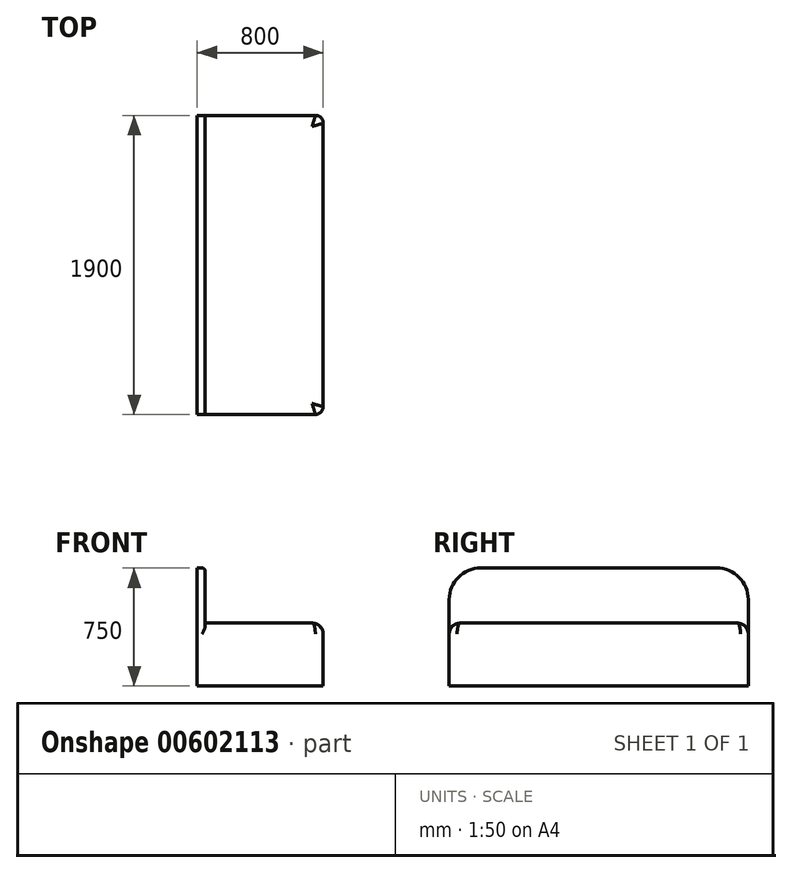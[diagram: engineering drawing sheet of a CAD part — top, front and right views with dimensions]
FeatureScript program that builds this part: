
annotation { "Feature Type Name" : "Feature", "Feature Type Description" : "" }
export const myFeature = defineFeature(function(context is Context, id is Id, definition is map)
    precondition{}
    {
        {
            var Q0;
            Q0=qCreatedBy(makeId("Top.planeOp"),FACE);
            var sketch = newSketch(context, id + "F0", { "sketchPlane" : qUnion([Q0])});
            skLineSegment(sketch, "E0.bottom", {"start": v(0, 0) * mm, "end": v(800, 0) * mm});
            skLineSegment(sketch, "E0.top", {"start": v(0, -1900) * mm, "end": v(800, -1900) * mm});
            skLineSegment(sketch, "E0.left", {"start": v(0, 0) * mm, "end": v(0, -1900) * mm});
            skLineSegment(sketch, "E0.right", {"start": v(800, 0) * mm, "end": v(800, -1900) * mm});
            skSolve(sketch);
        }
        {
            var Q0;
            Q0 = qSketchRegion(id + "F0", true);
            extrude(context, id + "F1", {"entities" : qUnion([Q0]), "depth" : 400 * mm, "offsetDistance" : 25 * mm});
        }
        {
            var Q0;
            Q0=makeQuery(id+"F1.opExtrude","CAP_FACE",FACE,{"disambiguationData":[OSD([sQuery(id+"F0.wireOp",EDGE,"E0.bottom"),sQuery(id+"F0.wireOp",EDGE,"E0.top"),sQuery(id+"F0.wireOp",EDGE,"E0.left"),sQuery(id+"F0.wireOp",EDGE,"E0.right")])],"isStart":false});
            var sketch = newSketch(context, id + "F2", { "sketchPlane" : qUnion([Q0])});
            skLineSegment(sketch, "E1.bottom", {"start": v(0, 0) * mm, "end": v(50, 0) * mm});
            skLineSegment(sketch, "E1.top", {"start": v(0, -1900) * mm, "end": v(50, -1900) * mm});
            skLineSegment(sketch, "E1.left", {"start": v(0, 0) * mm, "end": v(0, -1900) * mm});
            skLineSegment(sketch, "E1.right", {"start": v(50, 0) * mm, "end": v(50, -1900) * mm});
            skSolve(sketch);
        }
        {
            var Q0;
            Q0 = qSketchRegion(id + "F2", true);
            extrude(context, id + "F3", {"entities" : qUnion([Q0]), "operationType" : NewBodyOperationType.ADD, "depth" : 350 * mm, "offsetDistance" : 25 * mm});
        }
        {
            var Q0;
            Q0=makeQuery(id+"F1.opExtrude","SWEPT_EDGE",EDGE,{"disambiguationData":[OSD([sQuery(id+"F0.wireOp",EDGE,"E0.top"),sQuery(id+"F0.wireOp",EDGE,"E0.right")])]});
            var Q1;
            Q1=makeQuery(id+"F1.opExtrude","SWEPT_EDGE",EDGE,{"disambiguationData":[OSD([sQuery(id+"F0.wireOp",EDGE,"E0.bottom"),sQuery(id+"F0.wireOp",EDGE,"E0.right")])]});
            fillet(context, id + "F4", {"entities" : qUnion([Q0, Q1]), "radius" : 50 * mm, "tangentPropagation" : true, "allowEdgeOverflow" : false});
        }
        {
            var Q0;
            Q0=makeQuery(id+"F1.opExtrude","CAP_EDGE",EDGE,{"disambiguationData":[OSD([sQuery(id+"F0.wireOp",EDGE,"E0.top")])],"isStart":false});
            var Q1;
            Q1=makeQuery(id+"F1.opExtrude","CAP_EDGE",EDGE,{"disambiguationData":[OSD([sQuery(id+"F0.wireOp",EDGE,"E0.right")])],"isStart":false});
            var Q2;
            Q2=makeQuery(id+"F1.opExtrude","CAP_EDGE",EDGE,{"disambiguationData":[OSD([sQuery(id+"F0.wireOp",EDGE,"E0.bottom")])],"isStart":false});
            fillet(context, id + "F5", {"entities" : qUnion([Q0, Q1, Q2]), "radius" : 70 * mm, "tangentPropagation" : true, "allowEdgeOverflow" : false});
        }
        {
            var Q0;
            Q0=makeQuery(id+"F3.opExtrude","CAP_EDGE",EDGE,{"disambiguationData":[OSD([sQuery(id+"F2.wireOp",EDGE,"E1.top")])],"isStart":false});
            var Q1;
            Q1=makeQuery(id+"F3.opExtrude","CAP_EDGE",EDGE,{"disambiguationData":[OSD([sQuery(id+"F2.wireOp",EDGE,"E1.bottom")])],"isStart":false});
            fillet(context, id + "F6", {"entities" : qUnion([Q0, Q1]), "radius" : 200 * mm, "tangentPropagation" : true, "allowEdgeOverflow" : false});
        }
        {
            var Q0;
            Q0=makeQuery(id+"F3.opExtrude","SWEPT_EDGE",EDGE,{"disambiguationData":[OSD([sQuery(id+"F0.wireOp",EDGE,"E0.top"),sQuery(id+"F2.wireOp",EDGE,"E1.top"),sQuery(id+"F2.wireOp",EDGE,"E1.right")])]});
            var Q1;
            Q1=makeQuery(id+"F3.opExtrude","SWEPT_EDGE",EDGE,{"disambiguationData":[OSD([sQuery(id+"F0.wireOp",EDGE,"E0.bottom"),sQuery(id+"F2.wireOp",EDGE,"E1.bottom"),sQuery(id+"F2.wireOp",EDGE,"E1.right")])]});
            fillet(context, id + "F7", {"entities" : qUnion([Q0, Q1]), "radius" : 20 * mm, "tangentPropagation" : true, "allowEdgeOverflow" : false});
        }
    });
